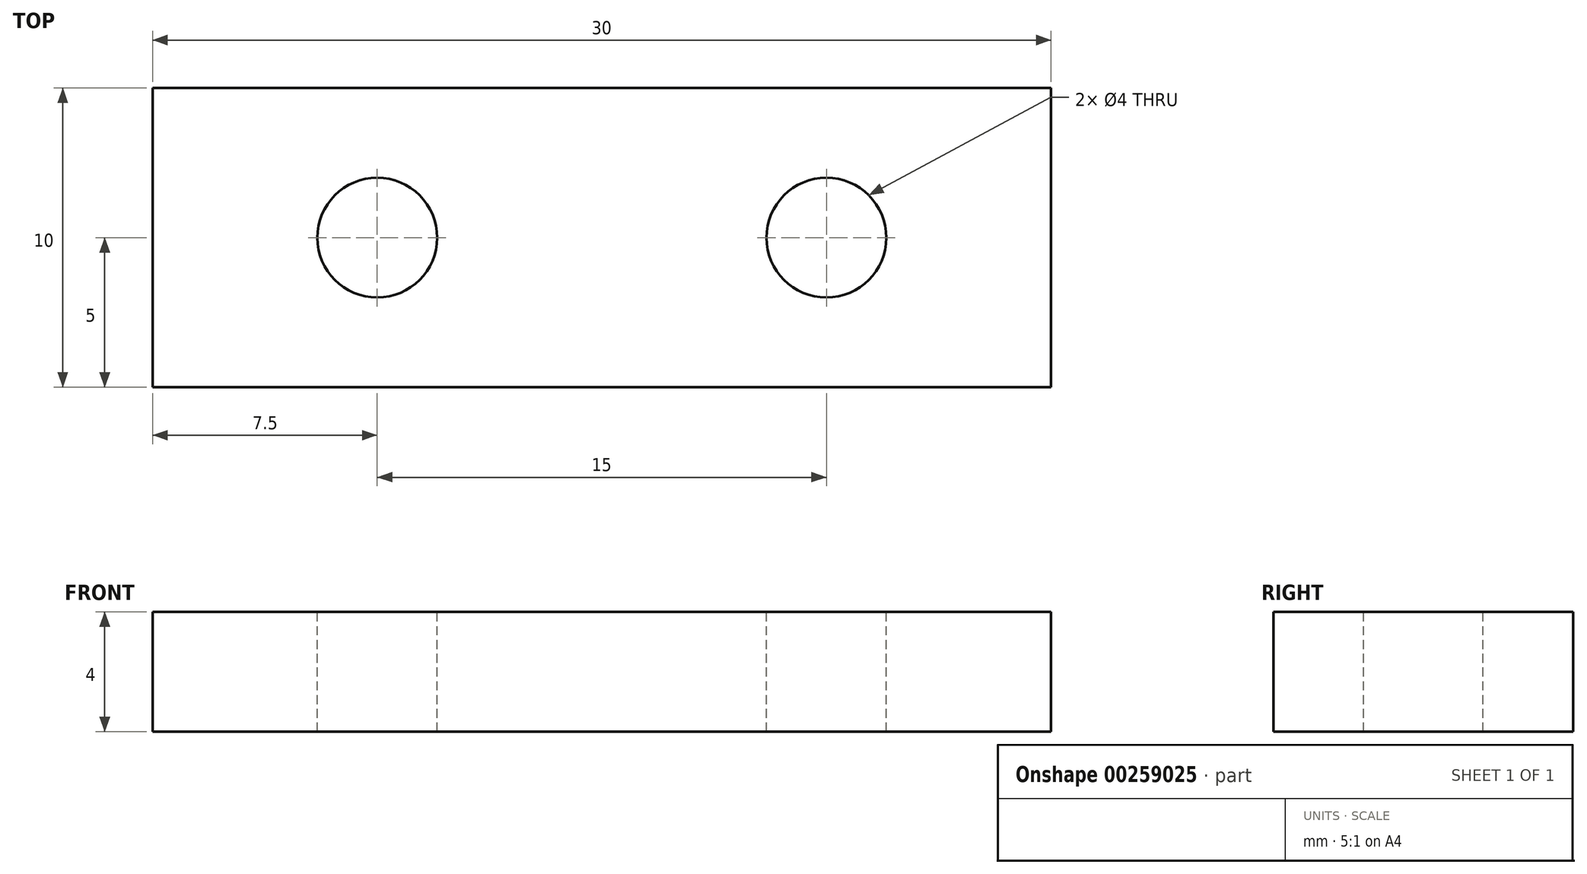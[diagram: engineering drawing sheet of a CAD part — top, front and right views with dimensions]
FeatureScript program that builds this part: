
annotation { "Feature Type Name" : "Feature", "Feature Type Description" : "" }
export const myFeature = defineFeature(function(context is Context, id is Id, definition is map)
    precondition{}
    {
        {
            var Q0;
            Q0=qCreatedBy(makeId("Top.planeOp"),FACE);
            var sketch = newSketch(context, id + "F0", { "sketchPlane" : qUnion([Q0])});
            skLineSegment(sketch, "E0.bottom", {"start": v(15, 5) * mm, "end": v(-15, 5) * mm});
            skLineSegment(sketch, "E0.top", {"start": v(15, -5) * mm, "end": v(-15, -5) * mm});
            skLineSegment(sketch, "E0.left", {"start": v(15, 5) * mm, "end": v(15, -5) * mm});
            skLineSegment(sketch, "E0.right", {"start": v(-15, 5) * mm, "end": v(-15, -5) * mm});
            skPoint(sketch, "E0.middle", {"position": v(0, 0) * mm});
            skSolve(sketch);
        }
        {
            var Q0;
            Q0=makeQuery(id+"F0.imprint","IMPRINT",FACE,{"disambiguationData":[TD([[makeQuery(id+"F0.imprint","IMPRINT",EDGE,{"derivedFrom":sQuery(id+"F0.wireOp",EDGE,"E0.bottom")}),1.0]])]});
            extrude(context, id + "F1", {"entities" : qUnion([Q0]), "depth" : 4 * mm, "offsetDistance" : 25 * mm});
        }
        {
            var Q0;
            Q0=makeQuery(id+"F1.opExtrude","CAP_FACE",FACE,{"disambiguationData":[OSD([sQuery(id+"F0.wireOp",EDGE,"E0.bottom"),sQuery(id+"F0.wireOp",EDGE,"E0.top"),sQuery(id+"F0.wireOp",EDGE,"E0.left"),sQuery(id+"F0.wireOp",EDGE,"E0.right")])],"isStart":true});
            var sketch = newSketch(context, id + "F2", { "sketchPlane" : qUnion([Q0])});
            skLineSegment(sketch, "E1", {"start": v(15, 0) * mm, "end": v(-15, 0) * mm, "construction": true});
            skPoint(sketch, "E2", {"position": v(-7.5, 0) * mm});
            skPoint(sketch, "E3", {"position": v(7.5, 0) * mm});
            skSolve(sketch);
        }
        {
            var Q0;
            Q0=sQuery(id+"F2.wireOp",VERTEX,"E2");
            var Q1;
            Q1=sQuery(id+"F2.wireOp",VERTEX,"E3");
            var Q2;
            Q2=makeQuery(id+"F1.opExtrude","SWEPT_BODY",BODY,{"disambiguationData":[OSD([sQuery(id+"F0.wireOp",EDGE,"E0.bottom"),sQuery(id+"F0.wireOp",EDGE,"E0.top"),sQuery(id+"F0.wireOp",EDGE,"E0.left"),sQuery(id+"F0.wireOp",EDGE,"E0.right")])]});
            hole(context, id + "F3", {"style" : HoleStyle.SIMPLE, "endStyle" : HoleEndStyle.THROUGH, "holeDiameter" : 4 * mm, "majorDiameter" : 5 * mm, "isTappedThrough" : true, "tappedDepth" : 12 * mm, "tapClearance" : 3, "startFromSketch" : true, "locations" : qUnion([Q0, Q1]), "scope" : qUnion([Q2])});
        }
    });
